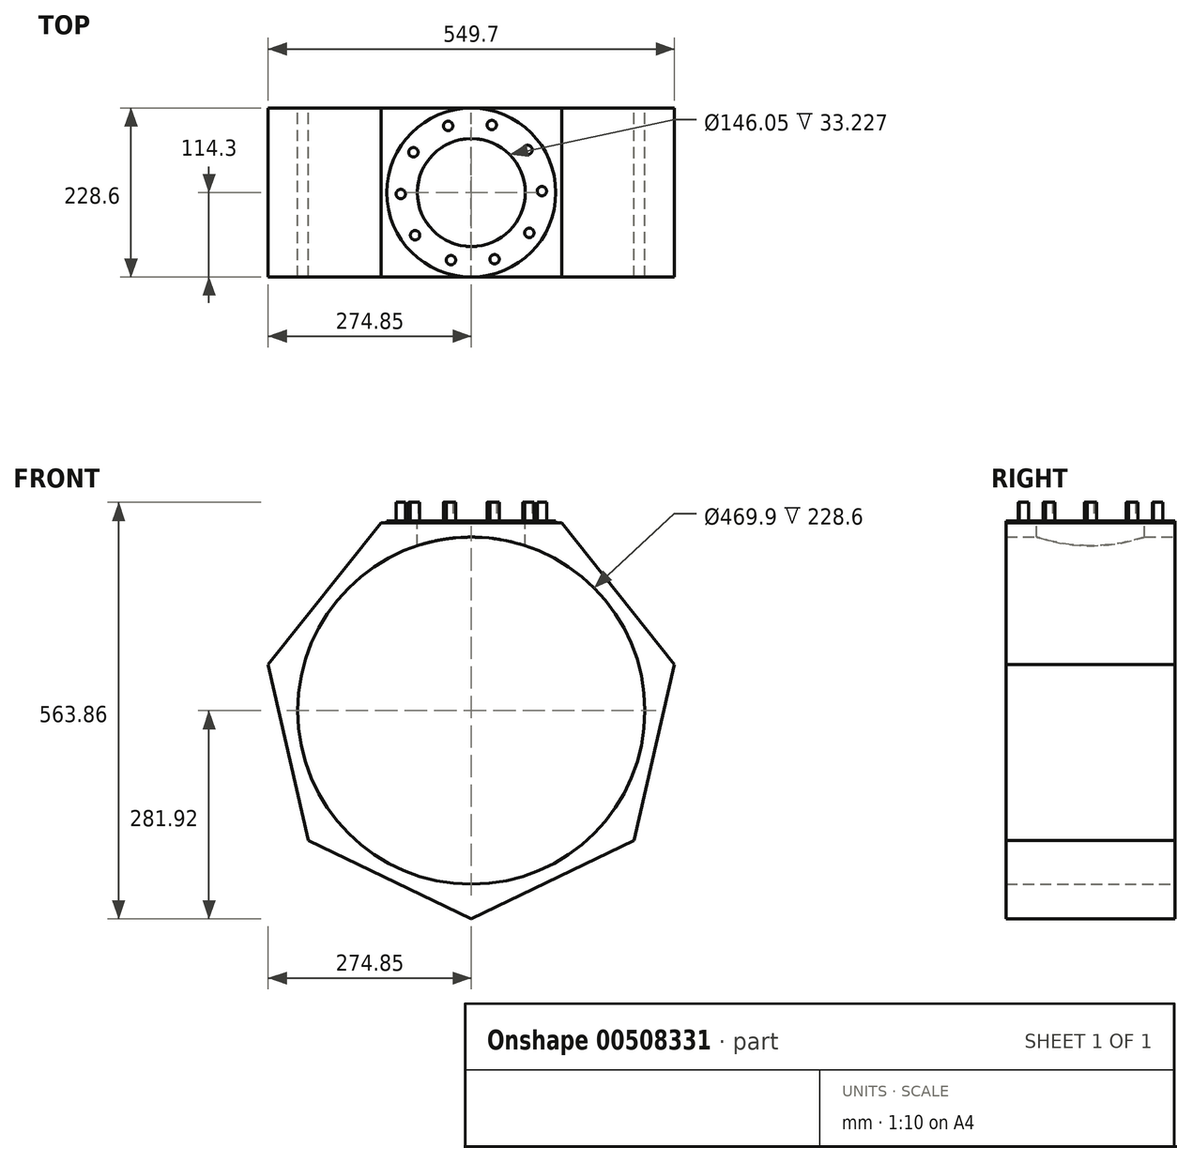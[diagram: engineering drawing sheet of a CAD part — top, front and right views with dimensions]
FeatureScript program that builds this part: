
annotation { "Feature Type Name" : "Feature", "Feature Type Description" : "" }
export const myFeature = defineFeature(function(context is Context, id is Id, definition is map)
    precondition{}
    {
        {
            var Q0;
            Q0=qCreatedBy(makeId("Front.planeOp"),FACE);
            var sketch = newSketch(context, id + "F0", { "sketchPlane" : qUnion([Q0])});
            skCircle(sketch, "E0.cCircle", {"center": v(0, 0) * mm, "radius": 241.3 * mm, "construction": true});
            skLineSegment(sketch, "E0.0", {"start": v(-116.2, 241.3) * mm, "end": v(116.2, 241.3) * mm});
            skLineSegment(sketch, "E0.1", {"start": v(116.2, 241.3) * mm, "end": v(261.1, 59.6) * mm});
            skLineSegment(sketch, "E0.2", {"start": v(261.1, 59.6) * mm, "end": v(209.4, -166.98) * mm});
            skLineSegment(sketch, "E0.3", {"start": v(209.4, -166.98) * mm, "end": v(0, -267.82) * mm});
            skLineSegment(sketch, "E0.4", {"start": v(0, -267.82) * mm, "end": v(-209.4, -166.98) * mm});
            skLineSegment(sketch, "E0.5", {"start": v(-209.4, -166.98) * mm, "end": v(-261.1, 59.6) * mm});
            skLineSegment(sketch, "E0.6", {"start": v(-261.1, 59.6) * mm, "end": v(-116.2, 241.3) * mm});
            skPoint(sketch, "E0.0.midPoint", {"position": v(0, 241.3) * mm});
            skLineSegment(sketch, "E1.0", {"start": v(-274.85, 62.73) * mm, "end": v(-122.32, 254) * mm});
            skLineSegment(sketch, "E1.1", {"start": v(-220.41, -175.77) * mm, "end": v(-274.85, 62.73) * mm});
            skLineSegment(sketch, "E1.2", {"start": v(122.32, 254) * mm, "end": v(274.85, 62.73) * mm});
            skLineSegment(sketch, "E1.3", {"start": v(274.85, 62.73) * mm, "end": v(220.41, -175.77) * mm});
            skLineSegment(sketch, "E1.4", {"start": v(220.41, -175.77) * mm, "end": v(0, -281.92) * mm});
            skLineSegment(sketch, "E1.5", {"start": v(-122.32, 254) * mm, "end": v(122.32, 254) * mm});
            skLineSegment(sketch, "E1.6", {"start": v(0, -281.92) * mm, "end": v(-220.41, -175.77) * mm});
            skSolve(sketch);
        }
        {
            var Q0;
            Q0=makeQuery(id+"F0.imprint","IMPRINT",FACE,{"disambiguationData":[TD([[makeQuery(id+"F0.imprint","IMPRINT",EDGE,{"derivedFrom":sQuery(id+"F0.wireOp",EDGE,"E0.0")}),1.0]])]});
            extrude(context, id + "F1", {"entities" : qUnion([Q0]), "depth" : 228.6 * mm, "offsetDistance" : 25.4 * mm, "symmetric" : true});
        }
        {
            var Q0;
            Q0=qCreatedBy(makeId("Front.planeOp"),FACE);
            var sketch = newSketch(context, id + "F2", { "sketchPlane" : qUnion([Q0])});
            skCircle(sketch, "E2", {"center": v(0, 0) * mm, "radius": 234.95 * mm});
            skLineSegment(sketch, "E3.0", {"start": v(-261.1, 59.6) * mm, "end": v(-116.2, 241.3) * mm});
            skLineSegment(sketch, "E4.0", {"start": v(-116.2, 241.3) * mm, "end": v(116.2, 241.3) * mm});
            skLineSegment(sketch, "E5.0", {"start": v(116.2, 241.3) * mm, "end": v(261.1, 59.6) * mm});
            skLineSegment(sketch, "E6.0", {"start": v(261.1, 59.6) * mm, "end": v(209.4, -166.98) * mm});
            skLineSegment(sketch, "E7.0", {"start": v(209.4, -166.98) * mm, "end": v(0, -267.82) * mm});
            skLineSegment(sketch, "E8.0", {"start": v(0, -267.82) * mm, "end": v(-209.4, -166.98) * mm});
            skLineSegment(sketch, "E9.0", {"start": v(-209.4, -166.98) * mm, "end": v(-261.1, 59.6) * mm});
            skSolve(sketch);
        }
        {
            var Q0;
            Q0=makeQuery(id+"F2.imprint","IMPRINT",FACE,{"disambiguationData":[TD([[makeQuery(id+"F2.imprint","IMPRINT",EDGE,{"derivedFrom":sQuery(id+"F2.wireOp",EDGE,"E2")}),-1.0]])]});
            extrude(context, id + "F3", {"entities" : qUnion([Q0]), "operationType" : NewBodyOperationType.ADD, "depth" : 228.6 * mm, "offsetDistance" : 25.4 * mm, "symmetric" : true});
        }
        {
            var Q0;
            Q0=makeQuery(id+"F1.opExtrude","SWEPT_FACE",FACE,{"disambiguationData":[OSD([sQuery(id+"F0.wireOp",EDGE,"E1.5")])]});
            var sketch = newSketch(context, id + "F4", { "sketchPlane" : qUnion([Q0])});
            skCircle(sketch, "E10", {"center": v(0, 0) * mm, "radius": 73.03 * mm});
            skSolve(sketch);
        }
        {
            var Q0;
            Q0=makeQuery(id+"F4.imprint","IMPRINT",FACE,{"disambiguationData":[TD([[makeQuery(id+"F4.imprint","IMPRINT",EDGE,{"derivedFrom":sQuery(id+"F4.wireOp",EDGE,"E10")}),1.0]])]});
            extrude(context, id + "F5", {"entities" : qUnion([Q0]), "operationType" : NewBodyOperationType.REMOVE, "oppositeDirection" : true, "depth" : 76.2 * mm, "offsetDistance" : 25.4 * mm});
        }
        {
            var Q0;
            Q0=makeQuery(id+"F1.opExtrude","SWEPT_FACE",FACE,{"disambiguationData":[OSD([sQuery(id+"F0.wireOp",EDGE,"E1.5")])]});
            var sketch = newSketch(context, id + "F6", { "sketchPlane" : qUnion([Q0])});
            skCircle(sketch, "E11.cCircle", {"center": v(0, 0) * mm, "radius": 85.1 * mm, "construction": true});
            skLineSegment(sketch, "E11.0", {"start": v(27.65, -85.1) * mm, "end": v(-27.65, -85.1) * mm});
            skLineSegment(sketch, "E11.1", {"start": v(-27.65, -85.1) * mm, "end": v(-72.38, -52.59) * mm});
            skLineSegment(sketch, "E11.2", {"start": v(-72.38, -52.59) * mm, "end": v(-89.47, 0) * mm});
            skLineSegment(sketch, "E11.3", {"start": v(-89.47, 0) * mm, "end": v(-72.38, 52.59) * mm});
            skLineSegment(sketch, "E11.4", {"start": v(-72.38, 52.59) * mm, "end": v(-27.65, 85.1) * mm});
            skLineSegment(sketch, "E11.5", {"start": v(-27.65, 85.09) * mm, "end": v(27.65, 85.1) * mm});
            skLineSegment(sketch, "E11.6", {"start": v(27.65, 85.1) * mm, "end": v(72.38, 52.59) * mm});
            skLineSegment(sketch, "E11.7", {"start": v(72.38, 52.59) * mm, "end": v(89.47, 0) * mm});
            skLineSegment(sketch, "E11.8", {"start": v(89.47, 0) * mm, "end": v(72.38, -52.59) * mm});
            skLineSegment(sketch, "E11.9", {"start": v(72.38, -52.59) * mm, "end": v(27.65, -85.09) * mm});
            skPoint(sketch, "E11.0.midPoint", {"position": v(0, -85.1) * mm});
            skCircle(sketch, "E12", {"center": v(0, 0) * mm, "radius": 114.3 * mm});
            skCircle(sketch, "E13", {"center": v(0, 0) * mm, "radius": 73.03 * mm});
            skSolve(sketch);
        }
        {
            var Q0;
            Q0=makeQuery(id+"F6.imprint","IMPRINT",FACE,{"disambiguationData":[TD([[makeQuery(id+"F6.imprint","IMPRINT",EDGE,{"derivedFrom":sQuery(id+"F6.wireOp",EDGE,"E11.0")}),1.0]])]});
            var Q1;
            Q1=makeQuery(id+"F6.imprint","IMPRINT",FACE,{"disambiguationData":[TD([[makeQuery(id+"F6.imprint","IMPRINT",EDGE,{"derivedFrom":sQuery(id+"F6.wireOp",EDGE,"E11.0")}),-1.0]])]});
            extrude(context, id + "F7", {"entities" : qUnion([Q0, Q1]), "operationType" : NewBodyOperationType.ADD, "depth" : 2.54 * mm, "offsetDistance" : 25.4 * mm});
        }
        {
            var Q0;
            Q0=makeQuery(id+"F7.opExtrude","CAP_FACE",FACE,{"disambiguationData":[OSD([sQuery(id+"F6.wireOp",EDGE,"E12"),sQuery(id+"F6.wireOp",EDGE,"E13")])],"isStart":false});
            var sketch = newSketch(context, id + "F8", { "sketchPlane" : qUnion([Q0])});
            skCircle(sketch, "E14.cCircle", {"center": v(0, 0) * mm, "radius": 91.44 * mm, "construction": true});
            skPoint(sketch, "E14.0.midPoint", {"position": v(0, 91.44) * mm});
            skCircle(sketch, "E15", {"center": v(27.65, 91.44) * mm, "radius": 6.35 * mm});
            skCircle(sketch, "E16.1.0", {"center": v(-31.38, 90.23) * mm, "radius": 6.35 * mm});
            skCircle(sketch, "E16.2.0", {"center": v(-78.42, 54.55) * mm, "radius": 6.35 * mm});
            skCircle(sketch, "E16.3.0", {"center": v(-95.5, -1.96) * mm, "radius": 6.35 * mm});
            skCircle(sketch, "E16.4.0", {"center": v(-76.11, -57.73) * mm, "radius": 6.35 * mm});
            skCircle(sketch, "E16.5.0", {"center": v(-27.65, -91.44) * mm, "radius": 6.35 * mm});
            skCircle(sketch, "E16.6.0", {"center": v(31.38, -90.23) * mm, "radius": 6.35 * mm});
            skCircle(sketch, "E16.7.0", {"center": v(78.42, -54.55) * mm, "radius": 6.35 * mm});
            skCircle(sketch, "E16.8.0", {"center": v(95.5, 1.96) * mm, "radius": 6.35 * mm});
            skCircle(sketch, "E16.9.0", {"center": v(76.11, 57.73) * mm, "radius": 6.35 * mm});
            skPoint(sketch, "E17.orphan", {"position": v(-27.65, 91.44) * mm});
            skPoint(sketch, "E18.orphan", {"position": v(72.38, 52.59) * mm});
            skPoint(sketch, "E19.orphan", {"position": v(89.47, 0) * mm});
            skPoint(sketch, "E20.orphan", {"position": v(72.38, -52.59) * mm});
            skPoint(sketch, "E21.orphan", {"position": v(27.65, -85.1) * mm});
            skPoint(sketch, "E22.orphan", {"position": v(-27.65, -85.1) * mm});
            skPoint(sketch, "E23.orphan", {"position": v(-72.38, -52.59) * mm});
            skPoint(sketch, "E24.orphan", {"position": v(-89.47, 0) * mm});
            skPoint(sketch, "E25.orphan", {"position": v(-72.38, 52.59) * mm});
            skSolve(sketch);
        }
        {
            var Q0;
            Q0=makeQuery(id+"F8.imprint","IMPRINT",FACE,{"disambiguationData":[TD([[makeQuery(id+"F8.imprint","IMPRINT",EDGE,{"derivedFrom":sQuery(id+"F8.wireOp",EDGE,"E16.1.0")}),1.0]])]});
            var Q1;
            Q1=makeQuery(id+"F8.imprint","IMPRINT",FACE,{"disambiguationData":[TD([[makeQuery(id+"F8.imprint","IMPRINT",EDGE,{"derivedFrom":sQuery(id+"F8.wireOp",EDGE,"E16.2.0")}),1.0]])]});
            var Q2;
            Q2=makeQuery(id+"F8.imprint","IMPRINT",FACE,{"disambiguationData":[TD([[makeQuery(id+"F8.imprint","IMPRINT",EDGE,{"derivedFrom":sQuery(id+"F8.wireOp",EDGE,"E16.3.0")}),1.0]])]});
            var Q3;
            Q3=makeQuery(id+"F8.imprint","IMPRINT",FACE,{"disambiguationData":[TD([[makeQuery(id+"F8.imprint","IMPRINT",EDGE,{"derivedFrom":sQuery(id+"F8.wireOp",EDGE,"E16.4.0")}),1.0]])]});
            var Q4;
            Q4=makeQuery(id+"F8.imprint","IMPRINT",FACE,{"disambiguationData":[TD([[makeQuery(id+"F8.imprint","IMPRINT",EDGE,{"derivedFrom":sQuery(id+"F8.wireOp",EDGE,"E16.5.0")}),1.0]])]});
            var Q5;
            Q5=makeQuery(id+"F8.imprint","IMPRINT",FACE,{"disambiguationData":[TD([[makeQuery(id+"F8.imprint","IMPRINT",EDGE,{"derivedFrom":sQuery(id+"F8.wireOp",EDGE,"E16.6.0")}),1.0]])]});
            var Q6;
            Q6=makeQuery(id+"F8.imprint","IMPRINT",FACE,{"disambiguationData":[TD([[makeQuery(id+"F8.imprint","IMPRINT",EDGE,{"derivedFrom":sQuery(id+"F8.wireOp",EDGE,"E16.7.0")}),1.0]])]});
            var Q7;
            Q7=makeQuery(id+"F8.imprint","IMPRINT",FACE,{"disambiguationData":[TD([[makeQuery(id+"F8.imprint","IMPRINT",EDGE,{"derivedFrom":sQuery(id+"F8.wireOp",EDGE,"E16.8.0")}),1.0]])]});
            var Q8;
            Q8=makeQuery(id+"F8.imprint","IMPRINT",FACE,{"disambiguationData":[TD([[makeQuery(id+"F8.imprint","IMPRINT",EDGE,{"derivedFrom":sQuery(id+"F8.wireOp",EDGE,"E16.9.0")}),1.0]])]});
            var Q9;
            Q9=makeQuery(id+"F8.imprint","IMPRINT",FACE,{"disambiguationData":[TD([[makeQuery(id+"F8.imprint","IMPRINT",EDGE,{"derivedFrom":sQuery(id+"F8.wireOp",EDGE,"E15")}),1.0]])]});
            extrude(context, id + "F9", {"entities" : qUnion([Q0, Q1, Q2, Q3, Q4, Q5, Q6, Q7, Q8, Q9]), "operationType" : NewBodyOperationType.ADD, "depth" : 25.4 * mm, "offsetDistance" : 25.4 * mm});
        }
    });
